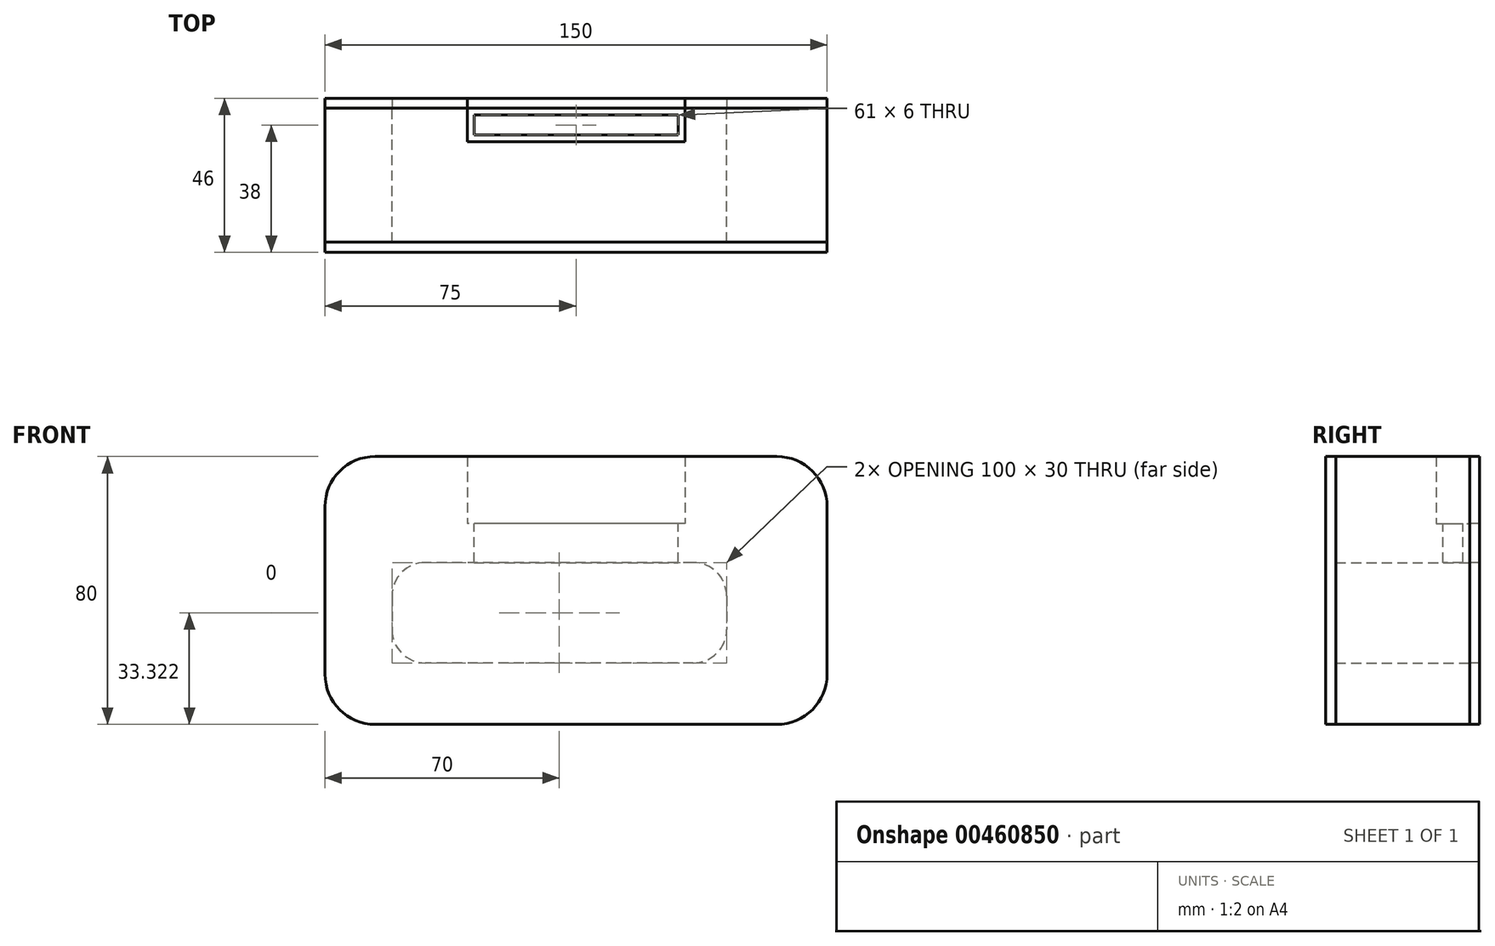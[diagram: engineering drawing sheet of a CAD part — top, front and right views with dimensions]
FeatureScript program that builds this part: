
annotation { "Feature Type Name" : "Feature", "Feature Type Description" : "" }
export const myFeature = defineFeature(function(context is Context, id is Id, definition is map)
    precondition{}
    {
        {
            var Q0;
            Q0=qCreatedBy(makeId("Top.planeOp"),FACE);
            var sketch = newSketch(context, id + "F0", { "sketchPlane" : qUnion([Q0])});
            skLineSegment(sketch, "E0.bottom", {"start": v(-75, 20) * mm, "end": v(75, 20) * mm});
            skLineSegment(sketch, "E0.top", {"start": v(-75, -20) * mm, "end": v(75, -20) * mm});
            skLineSegment(sketch, "E0.left", {"start": v(-75, 20) * mm, "end": v(-75, -20) * mm});
            skLineSegment(sketch, "E0.right", {"start": v(75, 20) * mm, "end": v(75, -20) * mm});
            skPoint(sketch, "E0.middle", {"position": v(0, 0) * mm});
            skSolve(sketch);
        }
        {
            var Q0;
            Q0 = qSketchRegion(id + "F0", true);
            extrude(context, id + "F1", {"entities" : qUnion([Q0]), "depth" : 80 * mm});
        }
        {
            var Q0;
            Q0=makeQuery(id+"F1.opExtrude","SWEPT_FACE",FACE,{"disambiguationData":[OSD([sQuery(id+"F0.wireOp",EDGE,"E0.bottom")])]});
            var sketch = newSketch(context, id + "F2", { "sketchPlane" : qUnion([Q0])});
            skLineSegment(sketch, "E1.bottom", {"start": v(-32.5, 80) * mm, "end": v(32.5, 80) * mm});
            skLineSegment(sketch, "E1.top", {"start": v(-32.5, 60) * mm, "end": v(32.5, 60) * mm});
            skLineSegment(sketch, "E1.left", {"start": v(-32.5, 80) * mm, "end": v(-32.5, 60) * mm});
            skLineSegment(sketch, "E1.right", {"start": v(32.5, 80) * mm, "end": v(32.5, 60) * mm});
            skSolve(sketch);
        }
        {
            var Q0;
            Q0=makeQuery(id+"F2.imprint","IMPRINT",FACE,{"disambiguationData":[TD([[makeQuery(id+"F2.imprint","IMPRINT",EDGE,{"derivedFrom":sQuery(id+"F2.wireOp",EDGE,"E1.bottom")}),1.0]])]});
            extrude(context, id + "F3", {"entities" : qUnion([Q0]), "operationType" : NewBodyOperationType.REMOVE, "oppositeDirection" : true, "depth" : 10 * mm});
        }
        {
            var Q0;
            Q0=makeQuery(id+"F1.opExtrude","SWEPT_FACE",FACE,{"disambiguationData":[OSD([sQuery(id+"F0.wireOp",EDGE,"E0.bottom")])]});
            var sketch = newSketch(context, id + "F4", { "sketchPlane" : qUnion([Q0])});
            skLineSegment(sketch, "E2.bottom", {"start": v(-35, 48.32) * mm, "end": v(45, 48.32) * mm});
            skLineSegment(sketch, "E2.top", {"start": v(-35, 18.32) * mm, "end": v(45, 18.32) * mm});
            skLineSegment(sketch, "E2.left", {"start": v(-45, 38.32) * mm, "end": v(-45, 28.32) * mm});
            skLineSegment(sketch, "E2.right", {"start": v(55, 38.32) * mm, "end": v(55, 28.32) * mm});
            skPoint(sketch, "E3.visualSharp", {"position": v(-45, 48.32) * mm});
            skArc(sketch, "E3.filletArc", {"start": v(-35, 48.32) * mm, "mid": v(-42.07, 45.4) * mm, "end": v(-45, 38.32) * mm});
            skPoint(sketch, "E4.visualSharp", {"position": v(-45, 18.32) * mm});
            skArc(sketch, "E4.filletArc", {"start": v(-45, 28.32) * mm, "mid": v(-42.07, 21.25) * mm, "end": v(-35, 18.32) * mm});
            skPoint(sketch, "E5.visualSharp", {"position": v(55, 18.32) * mm});
            skArc(sketch, "E5.filletArc", {"start": v(45, 18.32) * mm, "mid": v(52.07, 21.25) * mm, "end": v(55, 28.32) * mm});
            skPoint(sketch, "E6.visualSharp", {"position": v(55, 48.32) * mm});
            skArc(sketch, "E6.filletArc", {"start": v(55, 38.32) * mm, "mid": v(52.07, 45.4) * mm, "end": v(45, 48.32) * mm});
            skSolve(sketch);
        }
        {
            var Q0;
            Q0=makeQuery(id+"F4.imprint","IMPRINT",FACE,{"disambiguationData":[TD([[makeQuery(id+"F4.imprint","IMPRINT",EDGE,{"derivedFrom":sQuery(id+"F4.wireOp",EDGE,"E2.bottom")}),-1.0]])]});
            extrude(context, id + "F5", {"entities" : qUnion([Q0]), "operationType" : NewBodyOperationType.REMOVE, "oppositeDirection" : true, "depth" : 68.2 * mm});
        }
        {
            var Q0;
            Q0=makeQuery(id+"F3.boolean.opBoolean","COPY",FACE,{"derivedFrom":makeQuery(id+"F3.opExtrude","SWEPT_FACE",FACE,{"disambiguationData":[OSD([sQuery(id+"F2.wireOp",EDGE,"E1.top")])]})});
            var sketch = newSketch(context, id + "F6", { "sketchPlane" : qUnion([Q0])});
            skLineSegment(sketch, "E7.bottom", {"start": v(30.5, 12) * mm, "end": v(-30.5, 12) * mm});
            skLineSegment(sketch, "E7.top", {"start": v(30.5, 18) * mm, "end": v(-30.5, 18) * mm});
            skLineSegment(sketch, "E7.left", {"start": v(30.5, 12) * mm, "end": v(30.5, 18) * mm});
            skLineSegment(sketch, "E7.right", {"start": v(-30.5, 12) * mm, "end": v(-30.5, 18) * mm});
            skSolve(sketch);
        }
        {
            var Q0;
            Q0 = qSketchRegion(id + "F6", true);
            extrude(context, id + "F7", {"entities" : qUnion([Q0]), "operationType" : NewBodyOperationType.REMOVE, "oppositeDirection" : true, "depth" : 25 * mm});
        }
        {
            var Q0;
            Q0=makeQuery(id+"F1.opExtrude","SWEPT_FACE",FACE,{"disambiguationData":[OSD([sQuery(id+"F0.wireOp",EDGE,"E0.bottom")])]});
            var sketch = newSketch(context, id + "F8", { "sketchPlane" : qUnion([Q0])});
            skLineSegment(sketch, "E8.bottom", {"start": v(-75, 80) * mm, "end": v(75, 80) * mm});
            skLineSegment(sketch, "E8.top", {"start": v(-75, 0) * mm, "end": v(75, 0) * mm});
            skLineSegment(sketch, "E8.left", {"start": v(-75, 80) * mm, "end": v(-75, 0) * mm});
            skLineSegment(sketch, "E8.right", {"start": v(75, 80) * mm, "end": v(75, 0) * mm});
            skLineSegment(sketch, "E9.0", {"start": v(-35, 48.32) * mm, "end": v(45, 48.32) * mm});
            skArc(sketch, "E10.0", {"start": v(-35, 48.32) * mm, "mid": v(-42.07, 45.4) * mm, "end": v(-45, 38.32) * mm});
            skLineSegment(sketch, "E11.0", {"start": v(-45, 38.32) * mm, "end": v(-45, 28.32) * mm});
            skArc(sketch, "E12.0", {"start": v(-45, 28.32) * mm, "mid": v(-42.07, 21.25) * mm, "end": v(-35, 18.32) * mm});
            skLineSegment(sketch, "E13.0", {"start": v(-35, 18.32) * mm, "end": v(45, 18.32) * mm});
            skArc(sketch, "E14.0", {"start": v(45, 18.32) * mm, "mid": v(52.07, 21.25) * mm, "end": v(55, 28.32) * mm});
            skLineSegment(sketch, "E15.0", {"start": v(55, 38.32) * mm, "end": v(55, 28.32) * mm});
            skArc(sketch, "E16.0", {"start": v(55, 38.32) * mm, "mid": v(52.07, 45.4) * mm, "end": v(45, 48.32) * mm});
            skSolve(sketch);
        }
        {
            var Q0;
            Q0=makeQuery(id+"F8.imprint","IMPRINT",FACE,{"disambiguationData":[TD([[makeQuery(id+"F8.imprint","IMPRINT",EDGE,{"derivedFrom":sQuery(id+"F8.wireOp",EDGE,"E8.top")}),-1.0]])]});
            extrude(context, id + "F9", {"entities" : qUnion([Q0]), "depth" : 3 * mm});
        }
        {
            var Q0;
            Q0=makeQuery(id+"F1.opExtrude","SWEPT_FACE",FACE,{"disambiguationData":[OSD([sQuery(id+"F0.wireOp",EDGE,"E0.top")])]});
            var sketch = newSketch(context, id + "F10", { "sketchPlane" : qUnion([Q0])});
            skSolve(sketch);
        }
        {
            var Q0;
            {var subQ0=sQuery(id+"F0.wireOp",EDGE,"E0.top");Q0=makeQuery(id+"F10.imprint","IMPRINT",FACE,{"disambiguationData":[TD([[makeQuery(id+"F10.imprint","IMPRINT",EDGE,{"derivedFrom":makeQuery(id+"F1.opExtrude","CAP_EDGE",EDGE,{"disambiguationData":[OSD([subQ0])],"isStart":true})}),1.0]])]});}
            extrude(context, id + "F11", {"entities" : qUnion([Q0]), "depth" : 3 * mm});
        }
        {
            var Q0;
            Q0=makeQuery(id+"F1.opExtrude","SWEPT_FACE",FACE,{"disambiguationData":[OSD([sQuery(id+"F0.wireOp",EDGE,"E0.top")])]});
            var sketch = newSketch(context, id + "F12", { "sketchPlane" : qUnion([Q0])});
            skLineSegment(sketch, "E17.bottom", {"start": v(-75, 80) * mm, "end": v(75, 80) * mm});
            skLineSegment(sketch, "E17.top", {"start": v(-75, 0) * mm, "end": v(75, 0) * mm});
            skLineSegment(sketch, "E17.left", {"start": v(-75, 80) * mm, "end": v(-75, 0) * mm});
            skLineSegment(sketch, "E17.right", {"start": v(75, 80) * mm, "end": v(75, 0) * mm});
            skSolve(sketch);
        }
        {
            var Q0;
            Q0 = qSketchRegion(id + "F12", true);
            extrude(context, id + "F13", {"entities" : qUnion([Q0]), "depth" : 3 * mm});
        }
        {
            var Q0;
            Q0=makeQuery(id+"F11.opExtrude","SWEPT_BODY",BODY,{"disambiguationData":[OSD([sQuery(id+"F0.wireOp",EDGE,"E0.top"),sQuery(id+"F0.wireOp",EDGE,"E0.left"),sQuery(id+"F0.wireOp",EDGE,"E0.right"),sQuery(id+"F4.wireOp",EDGE,"E2.bottom"),sQuery(id+"F4.wireOp",EDGE,"E2.top"),sQuery(id+"F4.wireOp",EDGE,"E2.left"),sQuery(id+"F4.wireOp",EDGE,"E2.right"),sQuery(id+"F4.wireOp",EDGE,"E3.filletArc"),sQuery(id+"F4.wireOp",EDGE,"E4.filletArc"),sQuery(id+"F4.wireOp",EDGE,"E5.filletArc"),sQuery(id+"F4.wireOp",EDGE,"E6.filletArc")])]});
            deleteBodies(context, id + "F14", {"entities" : qUnion([Q0])});
        }
        {
            var Q0;
            Q0=makeQuery(id+"F1.opExtrude","CAP_EDGE",EDGE,{"disambiguationData":[OSD([sQuery(id+"F0.wireOp",EDGE,"E0.left")])],"isStart":false});
            fillet(context, id + "F15", {"entities" : qUnion([Q0]), "radius" : 15 * mm, "tangentPropagation" : true, "allowEdgeOverflow" : false});
        }
        {
            var Q0;
            Q0=makeQuery(id+"F1.opExtrude","CAP_EDGE",EDGE,{"disambiguationData":[OSD([sQuery(id+"F0.wireOp",EDGE,"E0.right")])],"isStart":false});
            fillet(context, id + "F16", {"entities" : qUnion([Q0]), "radius" : 15 * mm, "tangentPropagation" : true, "allowEdgeOverflow" : false});
        }
        {
            var Q0;
            Q0=makeQuery(id+"F1.opExtrude","CAP_EDGE",EDGE,{"disambiguationData":[OSD([sQuery(id+"F0.wireOp",EDGE,"E0.left")])],"isStart":true});
            fillet(context, id + "F17", {"entities" : qUnion([Q0]), "radius" : 15 * mm, "tangentPropagation" : true, "allowEdgeOverflow" : false});
        }
        {
            var Q0;
            Q0=makeQuery(id+"F1.opExtrude","CAP_EDGE",EDGE,{"disambiguationData":[OSD([sQuery(id+"F0.wireOp",EDGE,"E0.right")])],"isStart":true});
            fillet(context, id + "F18", {"entities" : qUnion([Q0]), "radius" : 15 * mm, "tangentPropagation" : true, "allowEdgeOverflow" : false});
        }
        {
            var Q0;
            Q0=makeQuery(id+"F9.opExtrude","SWEPT_EDGE",EDGE,{"disambiguationData":[OSD([sQuery(id+"F8.wireOp",EDGE,"E8.bottom"),sQuery(id+"F8.wireOp",EDGE,"E8.right")])]});
            fillet(context, id + "F19", {"entities" : qUnion([Q0]), "radius" : 15 * mm, "tangentPropagation" : true, "allowEdgeOverflow" : false});
        }
        {
            var Q0;
            Q0=makeQuery(id+"F9.opExtrude","SWEPT_EDGE",EDGE,{"disambiguationData":[OSD([sQuery(id+"F8.wireOp",EDGE,"E8.bottom"),sQuery(id+"F8.wireOp",EDGE,"E8.left")])]});
            fillet(context, id + "F20", {"entities" : qUnion([Q0]), "radius" : 15 * mm, "tangentPropagation" : true, "allowEdgeOverflow" : false});
        }
        {
            var Q0;
            Q0=makeQuery(id+"F9.opExtrude","SWEPT_EDGE",EDGE,{"disambiguationData":[OSD([sQuery(id+"F8.wireOp",EDGE,"E8.top"),sQuery(id+"F8.wireOp",EDGE,"E8.left")])]});
            fillet(context, id + "F21", {"entities" : qUnion([Q0]), "radius" : 15 * mm, "tangentPropagation" : true, "allowEdgeOverflow" : false});
        }
        {
            var Q0;
            Q0=makeQuery(id+"F9.opExtrude","SWEPT_EDGE",EDGE,{"disambiguationData":[OSD([sQuery(id+"F8.wireOp",EDGE,"E8.top"),sQuery(id+"F8.wireOp",EDGE,"E8.right")])]});
            fillet(context, id + "F22", {"entities" : qUnion([Q0]), "radius" : 15 * mm, "tangentPropagation" : true, "allowEdgeOverflow" : false});
        }
        {
            var Q0;
            Q0=makeQuery(id+"F13.opExtrude","SWEPT_EDGE",EDGE,{"disambiguationData":[OSD([sQuery(id+"F12.wireOp",EDGE,"E17.bottom"),sQuery(id+"F12.wireOp",EDGE,"E17.left")])]});
            fillet(context, id + "F23", {"entities" : qUnion([Q0]), "radius" : 15 * mm, "tangentPropagation" : true, "allowEdgeOverflow" : false});
        }
        {
            var Q0;
            Q0=makeQuery(id+"F13.opExtrude","SWEPT_EDGE",EDGE,{"disambiguationData":[OSD([sQuery(id+"F12.wireOp",EDGE,"E17.bottom"),sQuery(id+"F12.wireOp",EDGE,"E17.right")])]});
            fillet(context, id + "F24", {"entities" : qUnion([Q0]), "radius" : 15 * mm, "tangentPropagation" : true, "allowEdgeOverflow" : false});
        }
        {
            var Q0;
            Q0=makeQuery(id+"F13.opExtrude","SWEPT_EDGE",EDGE,{"disambiguationData":[OSD([sQuery(id+"F12.wireOp",EDGE,"E17.top"),sQuery(id+"F12.wireOp",EDGE,"E17.right")])]});
            fillet(context, id + "F25", {"entities" : qUnion([Q0]), "radius" : 15 * mm, "tangentPropagation" : true, "allowEdgeOverflow" : false});
        }
        {
            var Q0;
            Q0=makeQuery(id+"F13.opExtrude","SWEPT_EDGE",EDGE,{"disambiguationData":[OSD([sQuery(id+"F12.wireOp",EDGE,"E17.top"),sQuery(id+"F12.wireOp",EDGE,"E17.left")])]});
            fillet(context, id + "F26", {"entities" : qUnion([Q0]), "radius" : 15 * mm, "tangentPropagation" : true, "allowEdgeOverflow" : false});
        }
    });
